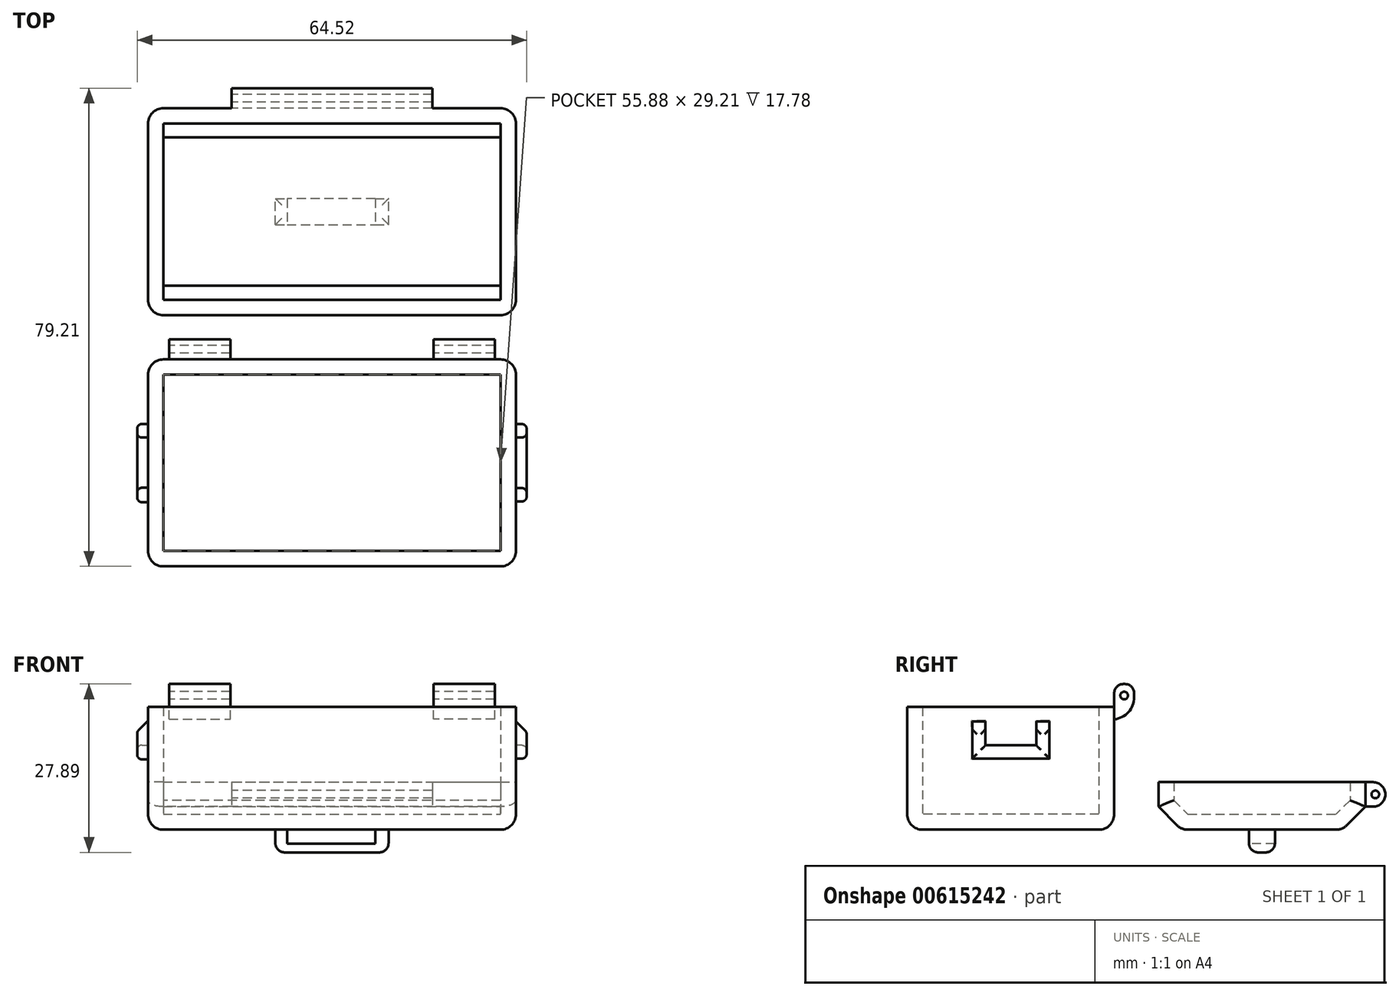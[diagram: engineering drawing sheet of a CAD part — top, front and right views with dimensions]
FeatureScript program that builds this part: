
annotation { "Feature Type Name" : "Feature", "Feature Type Description" : "" }
export const myFeature = defineFeature(function(context is Context, id is Id, definition is map)
    precondition{}
    {
        {
            var Q0;
            Q0=qCreatedBy(makeId("Top.planeOp"),FACE);
            var sketch = newSketch(context, id + "F0", { "sketchPlane" : qUnion([Q0])});
            skLineSegment(sketch, "E0.bottom", {"start": v(-30.48, 17.15) * mm, "end": v(30.48, 17.15) * mm});
            skLineSegment(sketch, "E0.top", {"start": v(-30.48, -17.14) * mm, "end": v(30.48, -17.14) * mm});
            skLineSegment(sketch, "E0.left", {"start": v(-30.48, 17.15) * mm, "end": v(-30.48, -17.14) * mm});
            skLineSegment(sketch, "E0.right", {"start": v(30.48, 17.15) * mm, "end": v(30.48, -17.14) * mm});
            skPoint(sketch, "E0.middle", {"position": v(0, 0) * mm});
            skSolve(sketch);
        }
        {
            var Q0;
            Q0=makeQuery(id+"F0.imprint","IMPRINT",FACE,{"disambiguationData":[TD([[makeQuery(id+"F0.imprint","IMPRINT",EDGE,{"derivedFrom":sQuery(id+"F0.wireOp",EDGE,"E0.bottom")}),-1.0]])]});
            extrude(context, id + "F1", {"entities" : qUnion([Q0]), "depth" : 20.32 * mm, "offsetDistance" : 25.4 * mm});
        }
        {
            var Q0;
            Q0=makeQuery(id+"F1.opExtrude","CAP_FACE",FACE,{"disambiguationData":[OSD([sQuery(id+"F0.wireOp",EDGE,"E0.bottom"),sQuery(id+"F0.wireOp",EDGE,"E0.top"),sQuery(id+"F0.wireOp",EDGE,"E0.left"),sQuery(id+"F0.wireOp",EDGE,"E0.right")])],"isStart":false});
            shell(context, id + "F2", {"entities" : qUnion([Q0]), "thickness" : 2.54 * mm});
        }
        {
            var Q0;
            Q0=makeQuery(id+"F1.opExtrude","CAP_EDGE",EDGE,{"disambiguationData":[OSD([sQuery(id+"F0.wireOp",EDGE,"E0.top")])],"isStart":true});
            var Q1;
            Q1=makeQuery(id+"F1.opExtrude","CAP_EDGE",EDGE,{"disambiguationData":[OSD([sQuery(id+"F0.wireOp",EDGE,"E0.left")])],"isStart":true});
            var Q2;
            Q2=makeQuery(id+"F1.opExtrude","CAP_EDGE",EDGE,{"disambiguationData":[OSD([sQuery(id+"F0.wireOp",EDGE,"E0.bottom")])],"isStart":true});
            var Q3;
            Q3=makeQuery(id+"F1.opExtrude","CAP_EDGE",EDGE,{"disambiguationData":[OSD([sQuery(id+"F0.wireOp",EDGE,"E0.right")])],"isStart":true});
            var Q4;
            Q4=makeQuery(id+"F1.opExtrude","SWEPT_EDGE",EDGE,{"disambiguationData":[OSD([sQuery(id+"F0.wireOp",EDGE,"E0.top"),sQuery(id+"F0.wireOp",EDGE,"E0.left")])]});
            var Q5;
            Q5=makeQuery(id+"F1.opExtrude","SWEPT_EDGE",EDGE,{"disambiguationData":[OSD([sQuery(id+"F0.wireOp",EDGE,"E0.bottom"),sQuery(id+"F0.wireOp",EDGE,"E0.left")])]});
            var Q6;
            Q6=makeQuery(id+"F1.opExtrude","SWEPT_EDGE",EDGE,{"disambiguationData":[OSD([sQuery(id+"F0.wireOp",EDGE,"E0.bottom"),sQuery(id+"F0.wireOp",EDGE,"E0.right")])]});
            var Q7;
            Q7=makeQuery(id+"F1.opExtrude","SWEPT_EDGE",EDGE,{"disambiguationData":[OSD([sQuery(id+"F0.wireOp",EDGE,"E0.top"),sQuery(id+"F0.wireOp",EDGE,"E0.right")])]});
            fillet(context, id + "F3", {"entities" : qUnion([Q0, Q1, Q2, Q3, Q4, Q5, Q6, Q7]), "radius" : 2.54 * mm, "tangentPropagation" : true, "allowEdgeOverflow" : false});
        }
        {
            var Q0;
            Q0=qCreatedBy(makeId("Top.planeOp"),FACE);
            var sketch = newSketch(context, id + "F4", { "sketchPlane" : qUnion([Q0])});
            skLineSegment(sketch, "E1.bottom", {"start": v(-30.48, 24.48) * mm, "end": v(30.48, 24.48) * mm});
            skLineSegment(sketch, "E1.top", {"start": v(-30.48, 58.77) * mm, "end": v(30.48, 58.77) * mm});
            skLineSegment(sketch, "E1.left", {"start": v(-30.48, 24.48) * mm, "end": v(-30.48, 58.77) * mm});
            skLineSegment(sketch, "E1.right", {"start": v(30.48, 24.48) * mm, "end": v(30.48, 58.77) * mm});
            skPoint(sketch, "E1.middle", {"position": v(0, 41.62) * mm});
            skSolve(sketch);
        }
        {
            var Q0;
            Q0=makeQuery(id+"F4.imprint","IMPRINT",FACE,{"disambiguationData":[TD([[makeQuery(id+"F4.imprint","IMPRINT",EDGE,{"derivedFrom":sQuery(id+"F4.wireOp",EDGE,"E1.bottom")}),1.0]])]});
            extrude(context, id + "F5", {"entities" : qUnion([Q0]), "depth" : 7.87 * mm, "offsetDistance" : 25.4 * mm});
        }
        {
            var Q0;
            Q0=makeQuery(id+"F5.opExtrude","CAP_EDGE",EDGE,{"disambiguationData":[OSD([sQuery(id+"F4.wireOp",EDGE,"E1.top")])],"isStart":true});
            var Q1;
            Q1=makeQuery(id+"F5.opExtrude","CAP_EDGE",EDGE,{"disambiguationData":[OSD([sQuery(id+"F4.wireOp",EDGE,"E1.bottom")])],"isStart":true});
            chamfer(context, id + "F6", {"entities" : qUnion([Q0, Q1]), "width" : 3.8 * mm, "tangentPropagation" : true});
        }
        {
            var Q0;
            Q0=makeQuery(id+"F5.opExtrude","CAP_FACE",FACE,{"disambiguationData":[OSD([sQuery(id+"F4.wireOp",EDGE,"E1.bottom"),sQuery(id+"F4.wireOp",EDGE,"E1.top"),sQuery(id+"F4.wireOp",EDGE,"E1.left"),sQuery(id+"F4.wireOp",EDGE,"E1.right")])],"isStart":false});
            shell(context, id + "F7", {"entities" : qUnion([Q0]), "thickness" : 2.54 * mm});
        }
        {
            var Q0;
            Q0=makeQuery(id+"F1.opExtrude","SWEPT_FACE",FACE,{"disambiguationData":[OSD([sQuery(id+"F0.wireOp",EDGE,"E0.bottom")])]});
            var sketch = newSketch(context, id + "F8", { "sketchPlane" : qUnion([Q0])});
            skLineSegment(sketch, "E2.bottom", {"start": v(27, 18.29) * mm, "end": v(16.83, 18.29) * mm});
            skLineSegment(sketch, "E2.top", {"start": v(27, 24.13) * mm, "end": v(16.83, 24.13) * mm});
            skLineSegment(sketch, "E2.left", {"start": v(27, 18.29) * mm, "end": v(27, 24.13) * mm});
            skLineSegment(sketch, "E2.right", {"start": v(16.83, 18.29) * mm, "end": v(16.83, 24.13) * mm});
            skLineSegment(sketch, "E3.bottom", {"start": v(-27, 18.29) * mm, "end": v(-16.84, 18.29) * mm});
            skLineSegment(sketch, "E3.top", {"start": v(-27, 24.13) * mm, "end": v(-16.84, 24.13) * mm});
            skLineSegment(sketch, "E3.left", {"start": v(-27, 18.29) * mm, "end": v(-27, 24.13) * mm});
            skLineSegment(sketch, "E3.right", {"start": v(-16.84, 18.29) * mm, "end": v(-16.84, 24.13) * mm});
            skSolve(sketch);
        }
        {
            var Q0;
            {var subQ0=sQuery(id+"F8.wireOp",EDGE,"E2.top");Q0=makeQuery(id+"F8.imprint","IMPRINT",FACE,{"disambiguationData":[TD([[makeQuery(id+"F8.imprint","IMPRINT",EDGE,{"derivedFrom":subQ0}),1.0]])]});}
            var Q1;
            {var subQ0=sQuery(id+"F8.wireOp",EDGE,"E2.bottom");Q1=makeQuery(id+"F8.imprint","IMPRINT",FACE,{"disambiguationData":[TD([[makeQuery(id+"F8.imprint","IMPRINT",EDGE,{"derivedFrom":subQ0}),-1.0]])]});}
            var Q2;
            {var subQ0=sQuery(id+"F8.wireOp",EDGE,"E3.bottom");Q2=makeQuery(id+"F8.imprint","IMPRINT",FACE,{"disambiguationData":[TD([[makeQuery(id+"F8.imprint","IMPRINT",EDGE,{"derivedFrom":subQ0}),1.0]])]});}
            var Q3;
            {var subQ0=sQuery(id+"F8.wireOp",EDGE,"E3.top");Q3=makeQuery(id+"F8.imprint","IMPRINT",FACE,{"disambiguationData":[TD([[makeQuery(id+"F8.imprint","IMPRINT",EDGE,{"derivedFrom":subQ0}),-1.0]])]});}
            extrude(context, id + "F9", {"entities" : qUnion([Q0, Q1, Q2, Q3]), "operationType" : NewBodyOperationType.ADD, "depth" : 3.3 * mm, "offsetDistance" : 25.4 * mm});
        }
        {
            var Q0;
            {var subQ0=sQuery(id+"F4.wireOp",EDGE,"E1.top");Q0=makeQuery(id+"F6.opChamfer","BLEND_EDGE",EDGE,{"blendedFrom":[makeQuery(id+"F5.opExtrude","CAP_EDGE",EDGE,{"disambiguationData":[OSD([subQ0])],"isStart":true}),makeQuery(id+"F5.opExtrude","CAP_FACE",FACE,{"disambiguationData":[OSD([sQuery(id+"F4.wireOp",EDGE,"E1.bottom"),subQ0,sQuery(id+"F4.wireOp",EDGE,"E1.left"),sQuery(id+"F4.wireOp",EDGE,"E1.right")])],"isStart":true})],"blendedInto":[makeQuery(id+"F5.opExtrude","CAP_FACE",FACE,{"disambiguationData":[OSD([sQuery(id+"F4.wireOp",EDGE,"E1.bottom"),subQ0,sQuery(id+"F4.wireOp",EDGE,"E1.left"),sQuery(id+"F4.wireOp",EDGE,"E1.right")])],"isStart":true})]});}
            var Q1;
            {var subQ0=sQuery(id+"F4.wireOp",EDGE,"E1.bottom");Q1=makeQuery(id+"F6.opChamfer","BLEND_EDGE",EDGE,{"blendedFrom":[makeQuery(id+"F5.opExtrude","CAP_EDGE",EDGE,{"disambiguationData":[OSD([subQ0])],"isStart":true}),makeQuery(id+"F5.opExtrude","CAP_FACE",FACE,{"disambiguationData":[OSD([subQ0,sQuery(id+"F4.wireOp",EDGE,"E1.top"),sQuery(id+"F4.wireOp",EDGE,"E1.left"),sQuery(id+"F4.wireOp",EDGE,"E1.right")])],"isStart":true})],"blendedInto":[makeQuery(id+"F5.opExtrude","CAP_FACE",FACE,{"disambiguationData":[OSD([subQ0,sQuery(id+"F4.wireOp",EDGE,"E1.top"),sQuery(id+"F4.wireOp",EDGE,"E1.left"),sQuery(id+"F4.wireOp",EDGE,"E1.right")])],"isStart":true})]});}
            var Q2;
            Q2=makeQuery(id+"F6.opChamfer","BLEND_EDGE",EDGE,{"blendedFrom":[makeQuery(id+"F5.opExtrude","CAP_EDGE",EDGE,{"disambiguationData":[OSD([sQuery(id+"F4.wireOp",EDGE,"E1.bottom")])],"isStart":true}),makeQuery(id+"F5.opExtrude","SWEPT_FACE",FACE,{"disambiguationData":[OSD([sQuery(id+"F4.wireOp",EDGE,"E1.right")])]})],"blendedInto":[makeQuery(id+"F5.opExtrude","SWEPT_FACE",FACE,{"disambiguationData":[OSD([sQuery(id+"F4.wireOp",EDGE,"E1.right")])]})]});
            var Q3;
            Q3=makeQuery(id+"F5.opExtrude","CAP_EDGE",EDGE,{"disambiguationData":[OSD([sQuery(id+"F4.wireOp",EDGE,"E1.right")])],"isStart":true});
            var Q4;
            Q4=makeQuery(id+"F6.opChamfer","BLEND_EDGE",EDGE,{"blendedFrom":[makeQuery(id+"F5.opExtrude","CAP_EDGE",EDGE,{"disambiguationData":[OSD([sQuery(id+"F4.wireOp",EDGE,"E1.top")])],"isStart":true}),makeQuery(id+"F5.opExtrude","SWEPT_FACE",FACE,{"disambiguationData":[OSD([sQuery(id+"F4.wireOp",EDGE,"E1.right")])]})],"blendedInto":[makeQuery(id+"F5.opExtrude","SWEPT_FACE",FACE,{"disambiguationData":[OSD([sQuery(id+"F4.wireOp",EDGE,"E1.right")])]})]});
            var Q5;
            Q5=makeQuery(id+"F6.opChamfer","BLEND_EDGE",EDGE,{"blendedFrom":[makeQuery(id+"F5.opExtrude","CAP_EDGE",EDGE,{"disambiguationData":[OSD([sQuery(id+"F4.wireOp",EDGE,"E1.top")])],"isStart":true}),makeQuery(id+"F5.opExtrude","SWEPT_FACE",FACE,{"disambiguationData":[OSD([sQuery(id+"F4.wireOp",EDGE,"E1.left")])]})],"blendedInto":[makeQuery(id+"F5.opExtrude","SWEPT_FACE",FACE,{"disambiguationData":[OSD([sQuery(id+"F4.wireOp",EDGE,"E1.left")])]})]});
            var Q6;
            Q6=makeQuery(id+"F5.opExtrude","CAP_EDGE",EDGE,{"disambiguationData":[OSD([sQuery(id+"F4.wireOp",EDGE,"E1.left")])],"isStart":true});
            var Q7;
            Q7=makeQuery(id+"F5.opExtrude","SWEPT_EDGE",EDGE,{"disambiguationData":[OSD([sQuery(id+"F4.wireOp",EDGE,"E1.top"),sQuery(id+"F4.wireOp",EDGE,"E1.left")])]});
            var Q8;
            Q8=makeQuery(id+"F6.opChamfer","BLEND_EDGE",EDGE,{"blendedFrom":[makeQuery(id+"F5.opExtrude","CAP_EDGE",EDGE,{"disambiguationData":[OSD([sQuery(id+"F4.wireOp",EDGE,"E1.bottom")])],"isStart":true}),makeQuery(id+"F5.opExtrude","SWEPT_FACE",FACE,{"disambiguationData":[OSD([sQuery(id+"F4.wireOp",EDGE,"E1.left")])]})],"blendedInto":[makeQuery(id+"F5.opExtrude","SWEPT_FACE",FACE,{"disambiguationData":[OSD([sQuery(id+"F4.wireOp",EDGE,"E1.left")])]})]});
            var Q9;
            Q9=makeQuery(id+"F5.opExtrude","SWEPT_EDGE",EDGE,{"disambiguationData":[OSD([sQuery(id+"F4.wireOp",EDGE,"E1.bottom"),sQuery(id+"F4.wireOp",EDGE,"E1.left")])]});
            var Q10;
            Q10=makeQuery(id+"F5.opExtrude","SWEPT_EDGE",EDGE,{"disambiguationData":[OSD([sQuery(id+"F4.wireOp",EDGE,"E1.bottom"),sQuery(id+"F4.wireOp",EDGE,"E1.right")])]});
            var Q11;
            Q11=makeQuery(id+"F5.opExtrude","SWEPT_EDGE",EDGE,{"disambiguationData":[OSD([sQuery(id+"F4.wireOp",EDGE,"E1.top"),sQuery(id+"F4.wireOp",EDGE,"E1.right")])]});
            fillet(context, id + "F10", {"entities" : qUnion([Q0, Q1, Q2, Q3, Q4, Q5, Q6, Q7, Q8, Q9, Q10, Q11]), "radius" : 2.54 * mm, "tangentPropagation" : true, "allowEdgeOverflow" : false});
        }
        {
            var Q0;
            Q0=makeQuery(id+"F9.opExtrude","SWEPT_FACE",FACE,{"disambiguationData":[OSD([sQuery(id+"F8.wireOp",EDGE,"E2.left")])]});
            var sketch = newSketch(context, id + "F11", { "sketchPlane" : qUnion([Q0])});
            skPoint(sketch, "E4", {"position": v(-18.8, 22.23) * mm});
            skPoint(sketch, "E4.positionSnap0", {"position": v(-17.15, 22.23) * mm});
            skPoint(sketch, "E4.positionSnap1", {"position": v(-18.8, 24.13) * mm});
            skSolve(sketch);
        }
        {
            var Q0;
            Q0=sQuery(id+"F11.wireOp",VERTEX,"E4");
            var Q1;
            Q1=makeQuery(id+"F1.opExtrude","SWEPT_BODY",BODY,{"disambiguationData":[OSD([sQuery(id+"F0.wireOp",EDGE,"E0.bottom"),sQuery(id+"F0.wireOp",EDGE,"E0.top"),sQuery(id+"F0.wireOp",EDGE,"E0.left"),sQuery(id+"F0.wireOp",EDGE,"E0.right")])]});
            hole(context, id + "F12", {"style" : HoleStyle.SIMPLE, "endStyle" : HoleEndStyle.THROUGH, "holeDiameter" : 1.27 * mm, "majorDiameter" : 6.35 * mm, "isTappedThrough" : true, "tappedDepth" : 12.7 * mm, "tapClearance" : 3, "locations" : qUnion([Q0]), "scope" : qUnion([Q1])});
        }
        {
            var Q0;
            Q0=makeQuery(id+"F5.opExtrude","CAP_FACE",FACE,{"disambiguationData":[OSD([sQuery(id+"F4.wireOp",EDGE,"E1.bottom"),sQuery(id+"F4.wireOp",EDGE,"E1.top"),sQuery(id+"F4.wireOp",EDGE,"E1.left"),sQuery(id+"F4.wireOp",EDGE,"E1.right")])],"isStart":true});
            var sketch = newSketch(context, id + "F13", { "sketchPlane" : qUnion([Q0])});
            skLineSegment(sketch, "E5.bottom", {"start": v(0, -41.62) * mm, "end": v(0, -41.62) * mm});
            skLineSegment(sketch, "E5.top", {"start": v(0, -66.19) * mm, "end": v(0, -66.19) * mm});
            skLineSegment(sketch, "E5.left", {"start": v(0, -41.62) * mm, "end": v(0, -66.19) * mm});
            skLineSegment(sketch, "E5.right", {"start": v(0, -41.62) * mm, "end": v(0, -66.19) * mm});
            skPoint(sketch, "E5.middle", {"position": v(0, -53.9) * mm});
            skPoint(sketch, "E5.cornerSnap0", {"position": v(0, -53.9) * mm});
            skPoint(sketch, "E5.cornerSnap1", {"position": v(27.94, -41.62) * mm});
            skLineSegment(sketch, "E6.bottom", {"start": v(-9.38, -39.46) * mm, "end": v(9.38, -39.46) * mm});
            skLineSegment(sketch, "E6.top", {"start": v(-9.38, -43.78) * mm, "end": v(9.38, -43.78) * mm});
            skLineSegment(sketch, "E6.left", {"start": v(-9.38, -39.46) * mm, "end": v(-9.38, -43.78) * mm});
            skLineSegment(sketch, "E6.right", {"start": v(9.38, -39.46) * mm, "end": v(9.38, -43.78) * mm});
            skPoint(sketch, "E6.middle", {"position": v(0, -41.62) * mm});
            skSolve(sketch);
        }
        {
            var Q0;
            Q0=makeQuery(id+"F13.imprint","IMPRINT",FACE,{"disambiguationData":[TD([[makeQuery(id+"F13.imprint","IMPRINT",EDGE,{"derivedFrom":sQuery(id+"F13.wireOp",EDGE,"E6.bottom")}),-1.0]])]});
            extrude(context, id + "F14", {"entities" : qUnion([Q0]), "operationType" : NewBodyOperationType.ADD, "depth" : 3.76 * mm, "offsetDistance" : 25.4 * mm});
        }
        {
            var Q0;
            Q0=makeQuery(id+"F14.opExtrude","SWEPT_FACE",FACE,{"disambiguationData":[OSD([sQuery(id+"F13.wireOp",EDGE,"E6.bottom")])]});
            var sketch = newSketch(context, id + "F15", { "sketchPlane" : qUnion([Q0])});
            skLineSegment(sketch, "E7.bottom", {"start": v(7.16, 0) * mm, "end": v(-7.43, 0) * mm});
            skLineSegment(sketch, "E7.top", {"start": v(7.16, -2.3) * mm, "end": v(-7.43, -2.3) * mm});
            skLineSegment(sketch, "E7.left", {"start": v(7.16, 0) * mm, "end": v(7.16, -2.3) * mm});
            skLineSegment(sketch, "E7.right", {"start": v(-7.43, 0) * mm, "end": v(-7.43, -2.3) * mm});
            skSolve(sketch);
        }
        {
            var Q0;
            Q0=makeQuery(id+"F15.imprint","IMPRINT",FACE,{"disambiguationData":[TD([[makeQuery(id+"F15.imprint","IMPRINT",EDGE,{"derivedFrom":sQuery(id+"F15.wireOp",EDGE,"E7.bottom")}),-1.0]])]});
            extrude(context, id + "F16", {"entities" : qUnion([Q0]), "operationType" : NewBodyOperationType.REMOVE, "oppositeDirection" : true, "depth" : 25.4 * mm, "offsetDistance" : 25.4 * mm});
        }
        {
            var Q0;
            Q0=makeQuery(id+"F14.opExtrude","CAP_EDGE",EDGE,{"disambiguationData":[OSD([sQuery(id+"F13.wireOp",EDGE,"E6.top")])],"isStart":false});
            var Q1;
            Q1=makeQuery(id+"F14.opExtrude","CAP_EDGE",EDGE,{"disambiguationData":[OSD([sQuery(id+"F13.wireOp",EDGE,"E6.bottom")])],"isStart":false});
            var Q2;
            Q2=makeQuery(id+"F14.opExtrude","CAP_EDGE",EDGE,{"disambiguationData":[OSD([sQuery(id+"F13.wireOp",EDGE,"E6.right")])],"isStart":false});
            var Q3;
            Q3=makeQuery(id+"F14.opExtrude","CAP_EDGE",EDGE,{"disambiguationData":[OSD([sQuery(id+"F13.wireOp",EDGE,"E6.left")])],"isStart":false});
            var Q4;
            Q4=makeQuery(id+"F9.opExtrude","CAP_EDGE",EDGE,{"disambiguationData":[OSD([sQuery(id+"F8.wireOp",EDGE,"E3.top")])],"isStart":false});
            var Q5;
            Q5=makeQuery(id+"F9.opExtrude","CAP_EDGE",EDGE,{"disambiguationData":[OSD([sQuery(id+"F8.wireOp",EDGE,"E3.top")])],"isStart":true});
            var Q6;
            Q6=makeQuery(id+"F9.opExtrude","CAP_EDGE",EDGE,{"disambiguationData":[OSD([sQuery(id+"F8.wireOp",EDGE,"E2.top")])],"isStart":false});
            var Q7;
            Q7=makeQuery(id+"F9.opExtrude","CAP_EDGE",EDGE,{"disambiguationData":[OSD([sQuery(id+"F8.wireOp",EDGE,"E2.top")])],"isStart":true});
            fillet(context, id + "F17", {"entities" : qUnion([Q0, Q1, Q2, Q3, Q4, Q5, Q6, Q7]), "radius" : 1.52 * mm, "tangentPropagation" : true, "allowEdgeOverflow" : false});
        }
        {
            var Q0;
            Q0=makeQuery(id+"F5.opExtrude","SWEPT_FACE",FACE,{"disambiguationData":[OSD([sQuery(id+"F4.wireOp",EDGE,"E1.top")])]});
            var sketch = newSketch(context, id + "F18", { "sketchPlane" : qUnion([Q0])});
            skLineSegment(sketch, "E8.bottom", {"start": v(16.64, 7.87) * mm, "end": v(-16.64, 7.87) * mm});
            skLineSegment(sketch, "E8.top", {"start": v(16.64, 3.81) * mm, "end": v(-16.64, 3.81) * mm});
            skLineSegment(sketch, "E8.left", {"start": v(16.64, 7.87) * mm, "end": v(16.64, 3.81) * mm});
            skLineSegment(sketch, "E8.right", {"start": v(-16.64, 7.87) * mm, "end": v(-16.64, 3.81) * mm});
            skSolve(sketch);
        }
        {
            var Q0;
            Q0=makeQuery(id+"F9.opExtrude","CAP_EDGE",EDGE,{"disambiguationData":[OSD([sQuery(id+"F8.wireOp",EDGE,"E2.bottom")])],"isStart":false});
            var Q1;
            Q1=makeQuery(id+"F9.opExtrude","CAP_EDGE",EDGE,{"disambiguationData":[OSD([sQuery(id+"F8.wireOp",EDGE,"E3.bottom")])],"isStart":false});
            fillet(context, id + "F19", {"entities" : qUnion([Q0, Q1]), "radius" : 3.68 * mm, "tangentPropagation" : true, "allowEdgeOverflow" : false});
        }
        {
            var Q0;
            Q0=makeQuery(id+"F18.imprint","IMPRINT",FACE,{"disambiguationData":[TD([[makeQuery(id+"F18.imprint","IMPRINT",EDGE,{"derivedFrom":sQuery(id+"F18.wireOp",EDGE,"E8.bottom")}),1.0]])]});
            extrude(context, id + "F20", {"entities" : qUnion([Q0]), "operationType" : NewBodyOperationType.ADD, "depth" : 3.3 * mm, "offsetDistance" : 25.4 * mm});
        }
        {
            var Q0;
            Q0=makeQuery(id+"F20.opExtrude","SWEPT_FACE",FACE,{"disambiguationData":[OSD([sQuery(id+"F18.wireOp",EDGE,"E8.left")])]});
            var sketch = newSketch(context, id + "F21", { "sketchPlane" : qUnion([Q0])});
            skPoint(sketch, "E9", {"position": v(-60.42, 5.84) * mm});
            skPoint(sketch, "E9.positionSnap0", {"position": v(-60.42, 3.8) * mm});
            skPoint(sketch, "E9.positionSnap1", {"position": v(-62.07, 5.84) * mm});
            skSolve(sketch);
        }
        {
            var Q0;
            Q0=sQuery(id+"F21.wireOp",VERTEX,"E9");
            var Q1;
            Q1=makeQuery(id+"F5.opExtrude","SWEPT_BODY",BODY,{"disambiguationData":[OSD([sQuery(id+"F4.wireOp",EDGE,"E1.bottom"),sQuery(id+"F4.wireOp",EDGE,"E1.top"),sQuery(id+"F4.wireOp",EDGE,"E1.left"),sQuery(id+"F4.wireOp",EDGE,"E1.right")])]});
            hole(context, id + "F22", {"style" : HoleStyle.SIMPLE, "endStyle" : HoleEndStyle.THROUGH, "holeDiameter" : 1.27 * mm, "majorDiameter" : 6.35 * mm, "isTappedThrough" : true, "tappedDepth" : 12.7 * mm, "tapClearance" : 3, "locations" : qUnion([Q0]), "scope" : qUnion([Q1])});
        }
        {
            var Q0;
            Q0=makeQuery(id+"F20.opExtrude","CAP_EDGE",EDGE,{"disambiguationData":[OSD([sQuery(id+"F18.wireOp",EDGE,"E8.bottom")])],"isStart":false});
            var Q1;
            Q1=makeQuery(id+"F20.opExtrude","CAP_EDGE",EDGE,{"disambiguationData":[OSD([sQuery(id+"F18.wireOp",EDGE,"E8.top")])],"isStart":false});
            fillet(context, id + "F23", {"entities" : qUnion([Q0, Q1]), "radius" : 2.02 * mm, "tangentPropagation" : true, "allowEdgeOverflow" : false});
        }
        {
            var Q0;
            Q0=makeQuery(id+"F1.opExtrude","SWEPT_FACE",FACE,{"disambiguationData":[OSD([sQuery(id+"F0.wireOp",EDGE,"E0.right")])]});
            var sketch = newSketch(context, id + "F24", { "sketchPlane" : qUnion([Q0])});
            skLineSegment(sketch, "E10.bottom", {"start": v(-6.39, 17.95) * mm, "end": v(6.43, 17.95) * mm});
            skLineSegment(sketch, "E10.top", {"start": v(-6.39, 11.78) * mm, "end": v(6.43, 11.78) * mm});
            skLineSegment(sketch, "E10.left", {"start": v(-6.39, 17.95) * mm, "end": v(-6.39, 11.78) * mm});
            skLineSegment(sketch, "E10.right", {"start": v(6.43, 17.95) * mm, "end": v(6.43, 11.78) * mm});
            skLineSegment(sketch, "E11.bottom", {"start": v(-4.18, 17.95) * mm, "end": v(4.22, 17.95) * mm});
            skLineSegment(sketch, "E11.top", {"start": v(-4.18, 13.99) * mm, "end": v(4.22, 13.99) * mm});
            skLineSegment(sketch, "E11.left", {"start": v(-4.18, 17.95) * mm, "end": v(-4.18, 13.99) * mm});
            skLineSegment(sketch, "E11.right", {"start": v(4.22, 17.95) * mm, "end": v(4.22, 13.99) * mm});
            skSolve(sketch);
        }
        {
            var Q0;
            Q0=makeQuery(id+"F1.opExtrude","SWEPT_FACE",FACE,{"disambiguationData":[OSD([sQuery(id+"F0.wireOp",EDGE,"E0.left")])]});
            var sketch = newSketch(context, id + "F25", { "sketchPlane" : qUnion([Q0])});
            skLineSegment(sketch, "E12.bottom", {"start": v(-6.45, 18.05) * mm, "end": v(6.51, 18.05) * mm});
            skLineSegment(sketch, "E12.top", {"start": v(-6.45, 11.63) * mm, "end": v(6.51, 11.63) * mm});
            skLineSegment(sketch, "E12.left", {"start": v(-6.45, 18.05) * mm, "end": v(-6.45, 11.63) * mm});
            skLineSegment(sketch, "E12.right", {"start": v(6.51, 18.05) * mm, "end": v(6.51, 11.63) * mm});
            skLineSegment(sketch, "E13.bottom", {"start": v(-4.2, 18.05) * mm, "end": v(4.13, 18.05) * mm});
            skLineSegment(sketch, "E13.top", {"start": v(-4.2, 14.02) * mm, "end": v(4.13, 14.02) * mm});
            skLineSegment(sketch, "E13.left", {"start": v(-4.2, 18.05) * mm, "end": v(-4.2, 14.02) * mm});
            skLineSegment(sketch, "E13.right", {"start": v(4.13, 18.05) * mm, "end": v(4.13, 14.02) * mm});
            skSolve(sketch);
        }
        {
            var Q0;
            Q0=makeQuery(id+"F25.imprint","IMPRINT",FACE,{"disambiguationData":[TD([[makeQuery(id+"F25.imprint","IMPRINT",EDGE,{"derivedFrom":sQuery(id+"F25.wireOp",EDGE,"E12.top")}),1.0]])]});
            extrude(context, id + "F26", {"entities" : qUnion([Q0]), "operationType" : NewBodyOperationType.ADD, "depth" : 1.78 * mm, "offsetDistance" : 25.4 * mm});
        }
        {
            var Q0;
            {var subQ0=sQuery(id+"F25.wireOp",EDGE,"E12.bottom");Q0=makeQuery(id+"F26.opExtrude","CAP_EDGE",EDGE,{"disambiguationData":[OSD([subQ0]),TDD([makeQuery(id+"F25.imprint","IMPRINT",EDGE,{"disambiguationData":[TD([[makeQuery(id+"F25.imprint","INTERSECT",VERTEX,{"derivedFrom":[subQ0,sQuery(id+"F25.wireOp",EDGE,"E12.left")]}),-1.0]])],"derivedFrom":subQ0})])],"isStart":false});}
            var Q1;
            {var subQ0=sQuery(id+"F25.wireOp",EDGE,"E12.bottom");Q1=makeQuery(id+"F26.opExtrude","CAP_EDGE",EDGE,{"disambiguationData":[OSD([subQ0]),TDD([makeQuery(id+"F25.imprint","IMPRINT",EDGE,{"disambiguationData":[TD([[makeQuery(id+"F25.imprint","INTERSECT",VERTEX,{"derivedFrom":[subQ0,sQuery(id+"F25.wireOp",EDGE,"E12.right")]}),1.0]])],"derivedFrom":subQ0})])],"isStart":false});}
            chamfer(context, id + "F27", {"entities" : qUnion([Q0, Q1]), "width" : 1.78 * mm, "tangentPropagation" : true});
        }
        {
            var Q0;
            Q0=makeQuery(id+"F26.opExtrude","CAP_FACE",FACE,{"disambiguationData":[OSD([sQuery(id+"F25.wireOp",EDGE,"E12.bottom"),sQuery(id+"F25.wireOp",EDGE,"E12.top"),sQuery(id+"F25.wireOp",EDGE,"E12.left"),sQuery(id+"F25.wireOp",EDGE,"E12.right"),sQuery(id+"F25.wireOp",EDGE,"E13.top"),sQuery(id+"F25.wireOp",EDGE,"E13.left"),sQuery(id+"F25.wireOp",EDGE,"E13.right")])],"isStart":false});
            fillet(context, id + "F28", {"entities" : qUnion([Q0]), "radius" : 0.76 * mm, "tangentPropagation" : true, "allowEdgeOverflow" : false});
        }
        {
            var Q0;
            Q0=makeQuery(id+"F24.imprint","IMPRINT",FACE,{"disambiguationData":[TD([[makeQuery(id+"F24.imprint","IMPRINT",EDGE,{"derivedFrom":sQuery(id+"F24.wireOp",EDGE,"E10.top")}),1.0]])]});
            extrude(context, id + "F29", {"entities" : qUnion([Q0]), "operationType" : NewBodyOperationType.ADD, "depth" : 1.78 * mm, "offsetDistance" : 25.4 * mm});
        }
        {
            var Q0;
            {var subQ0=sQuery(id+"F24.wireOp",EDGE,"E10.bottom");Q0=makeQuery(id+"F29.opExtrude","CAP_EDGE",EDGE,{"disambiguationData":[OSD([subQ0]),TDD([makeQuery(id+"F24.imprint","IMPRINT",EDGE,{"disambiguationData":[TD([[makeQuery(id+"F24.imprint","INTERSECT",VERTEX,{"derivedFrom":[subQ0,sQuery(id+"F24.wireOp",EDGE,"E10.left")]}),-1.0]])],"derivedFrom":subQ0})])],"isStart":false});}
            var Q1;
            {var subQ0=sQuery(id+"F24.wireOp",EDGE,"E10.bottom");Q1=makeQuery(id+"F29.opExtrude","CAP_EDGE",EDGE,{"disambiguationData":[OSD([subQ0]),TDD([makeQuery(id+"F24.imprint","IMPRINT",EDGE,{"disambiguationData":[TD([[makeQuery(id+"F24.imprint","INTERSECT",VERTEX,{"derivedFrom":[subQ0,sQuery(id+"F24.wireOp",EDGE,"E10.right")]}),1.0]])],"derivedFrom":subQ0})])],"isStart":false});}
            chamfer(context, id + "F30", {"entities" : qUnion([Q0, Q1]), "width" : 1.78 * mm, "tangentPropagation" : true});
        }
        {
            var Q0;
            Q0=makeQuery(id+"F29.opExtrude","CAP_FACE",FACE,{"disambiguationData":[OSD([sQuery(id+"F24.wireOp",EDGE,"E10.bottom"),sQuery(id+"F24.wireOp",EDGE,"E10.top"),sQuery(id+"F24.wireOp",EDGE,"E10.left"),sQuery(id+"F24.wireOp",EDGE,"E10.right"),sQuery(id+"F24.wireOp",EDGE,"E11.top"),sQuery(id+"F24.wireOp",EDGE,"E11.left"),sQuery(id+"F24.wireOp",EDGE,"E11.right")])],"isStart":false});
            fillet(context, id + "F31", {"entities" : qUnion([Q0]), "radius" : 0.76 * mm, "tangentPropagation" : true, "allowEdgeOverflow" : false});
        }
    });
